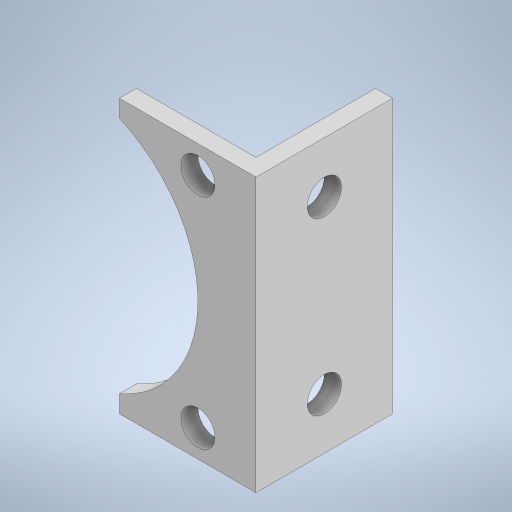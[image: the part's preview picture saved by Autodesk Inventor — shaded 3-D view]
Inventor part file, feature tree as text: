
AUTODESK INVENTOR PART (.ipt)
format: ipt  version: 2023 (Build 270158000, 158)  size: 251,904 bytes
history: native  units: in
note: dims shown in document units (in); Inventor stores cm internally (conversion verified against a paired STEP export)
features: extrude x3, sketch x3
ambient origin geometry x8: Origin, YZ Plane, XZ Plane, XY Plane, X Axis, Y Axis, Z Axis, Center Point
bodies: Solid1 (feature_tree)
feature tree (6):
  extrude  "Extrusion1"  Depth=0.125in
  extrude  "Extrusion2"  Depth=0.875in
  extrude  "Extrusion3"  Depth=2.0in
  sketch  "Sketch1"  dims[d0=1.0in d1=0.125in]
  sketch  "Sketch2"  dims[d2=0.875in d3=0.875in]
  sketch  "Sketch3"  dims[d4=2.0in d5=0.0in d9=0.25in d10=0.25in d13=2.5in d14=0.0in d18=2.5in d19=0.0in]
